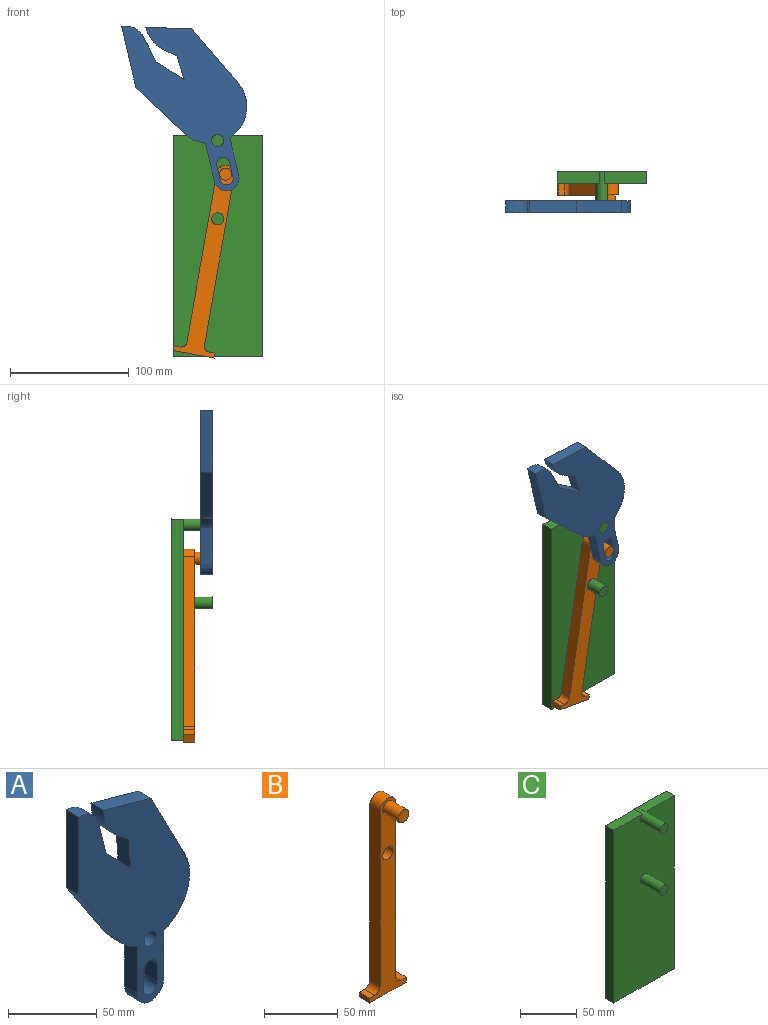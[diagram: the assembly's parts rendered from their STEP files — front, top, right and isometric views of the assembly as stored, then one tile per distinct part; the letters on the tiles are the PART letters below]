
ASSEMBLY  parts=3 mates=3
PART A: 23 faces, bbox 88.1x10x155.2 mm
  f0: plane 12.5x10mm, normal (-1,0,0), area 125mm2, adj f1,f18,f19,f20
  f1: cylinder r=5.5mm len=11mm, axis (0,1,0), area 172.8mm2, adj f0,f2,f19,f20
  f2: plane 12.5x10mm, normal (1,0,0), area 125mm2, adj f1,f18,f19,f20
  f3: plane 32.76x10mm, normal (1,0,0), area 327.6mm2, adj f4,f17,f19,f20
  f4: cylinder r=31.21mm len=43.74mm, axis (0,1,0), area 532.3mm2, adj f3,f5,f19,f20
  f5: plane 52.57x27.24mm, normal (0.89,0,0.46), area 592.1mm2, adj f4,f6,f19,f20
  f6: plane 37.75x10.5mm, normal (0.27,0,0.96), area 391.9mm2, adj f5,f19,f20,f22
  f7: plane 10x8.94mm, normal (-0.62,0,-0.79), area 113.6mm2, adj f8,f19,f20,f22
  f8: plane 20.72x10mm, normal (-1,0,-0.06), area 207.5mm2, adj f7,f9,f19,f20
  f9: plane 20.53x19.65mm, normal (0.72,0,0.69), area 284.1mm2, adj f8,f10,f19,f20
  f10: plane 22.63x10mm, normal (0.97,0,0.24), area 232.9mm2, adj f9,f19,f20,f21
  f11: plane 53.29x10mm, normal (-1,0,0), area 532.9mm2, adj f12,f19,f20,f21
  f12: plane 46.52x30.9mm, normal (-0.83,0,-0.55), area 558.5mm2, adj f11,f13,f19,f20
  f13: plane 10x1.21mm, normal (-0.82,0,-0.57), area 14.8mm2, adj f12,f14,f19,f20
  f14: cylinder r=31.21mm len=14.64mm, axis (0,1,0), area 185.3mm2, adj f13,f15,f19,f20
  f15: plane 32.76x10mm, normal (-1,0,0), area 327.6mm2, adj f14,f17,f19,f20
  f16: cylinder r=5mm len=10mm, axis (0,1,0), area 314.2mm2, adj f19,f20
  f17: cylinder r=10.5mm len=21mm, axis (0,1,0), area 329.9mm2, adj f3,f15,f19,f20
  f18: cylinder r=5.5mm len=11mm, axis (0,1,0), area 172.8mm2, adj f0,f2,f19,f20
  f19: plane 155.2x88.1mm, normal (0,-1,0), area 6788.4mm2, adj f0,f1,f2,f3,f4,f5,f6,f7
  f20: plane 155.2x88.1mm, normal (0,1,0), area 6788.4mm2, adj f0,f1,f2,f3,f4,f5,f6,f7
  f21: cylinder r=16.42mm len=15.85mm, axis (0,-1,0), area 217.7mm2, adj f10,f11,f19,f20
  f22: cylinder r=29.45mm len=22.85mm, axis (0,1,0), area 263.4mm2, adj f6,f7,f19,f20
PART B: 15 faces, bbox 35x25x161.6 mm
  f0: plane 10x5mm, normal (0,0,1), area 50mm2, adj f7,f9,f10,f13
  f1: plane 145x10mm, normal (1,0,0), area 1450mm2, adj f2,f9,f10,f13
  f2: cylinder r=7.5mm len=15mm, axis (0,1,0), area 235.6mm2, adj f1,f3,f9,f10
  f3: plane 145x10mm, normal (-1,0,0), area 1450mm2, adj f2,f9,f10,f14
  f4: plane 10x5mm, normal (0,0,1), area 50mm2, adj f5,f9,f10,f14
  f5: plane 10x3.94mm, normal (-1,0,0), area 39.4mm2, adj f4,f6,f9,f10
  f6: plane 35x10mm, normal (0,0,-1), area 350mm2, adj f5,f7,f9,f10
  f7: plane 10x4.11mm, normal (1,0,0), area 41.1mm2, adj f0,f6,f9,f10
  f8: cylinder r=5mm len=10mm, axis (0,1,0), area 314.2mm2, adj f9,f10
  f9: plane 161.61x35mm, normal (0,-1,0), area 2332.8mm2, adj f0,f1,f2,f3,f4,f5,f6,f7
  f10: plane 161.61x35mm, normal (0,1,0), area 2411.4mm2, adj f0,f1,f2,f3,f4,f5,f6,f7
  f11: cylinder r=5mm len=15mm, axis (0,1,0), area 471.2mm2, adj f9,f12
  f12: plane 10x10mm, normal (0,-1,0), area 78.5mm2, adj f11
  f13: cylinder r=5mm len=10mm, axis (0,1,0), area 78.5mm2, adj f0,f1,f9,f10
  f14: cylinder r=5mm len=10mm, axis (0,-1,0), area 78.5mm2, adj f3,f4,f9,f10
PART C: 11 faces, bbox 75.2x35x187 mm
  f0: plane 186.51x10mm, normal (1,0,0), area 1865.1mm2, adj f1,f5,f6,f7
  f1: plane 35.46x10mm, normal (0,0,1), area 354.6mm2, adj f0,f2,f6,f7
  f2: cylinder r=5mm len=35mm, axis (0,-1,0), area 828.6mm2, adj f1,f3,f6,f7,f10
  f3: plane 35.49x10mm, normal (0,0,1), area 354.9mm2, adj f2,f4,f6,f7
  f4: plane 186.15x10mm, normal (-1,0,0), area 1861.5mm2, adj f3,f5,f6,f7
  f5: plane 75.14x10mm, normal (0,0,-1), area 751.4mm2, adj f0,f4,f6,f7
  f6: plane 186.97x75.19mm, normal (0,1,0), area 14001.1mm2, adj f0,f1,f2,f3,f4,f5
  f7: plane 186.51x75.19mm, normal (0,-1,0), area 13844mm2, adj f0,f1,f2,f3,f4,f5,f8
  f8: cylinder r=5mm len=25mm, axis (0,1,0), area 785.4mm2, adj f7,f9
  f9: plane 10x10mm, normal (0,-1,0), area 78.5mm2, adj f8
  f10: plane 10x10mm, normal (0,-1,0), area 78.5mm2, adj f2
PLACE A rot(axis=(0,-1,0),13.2deg) t=(-71.32,-62,143.78)mm
PLACE B rot(axis=(0,1,0),10deg) t=(-101.12,-47,141.65)mm
PLACE C t=(-94.72,-47,141.09)mm fixed
MATE pin_slot B.f11 <-> A.f18  axis (0,-1,0) through (-88.09,-72,215.51)mm
MATE revolute B.f8 <-> C.f8  axis (0,1,0) through (-94.72,-47,177.93)mm
MATE revolute C.f2 <-> A.f16  axis (0,-1,0) through (-94.72,-72,243.85)mm
